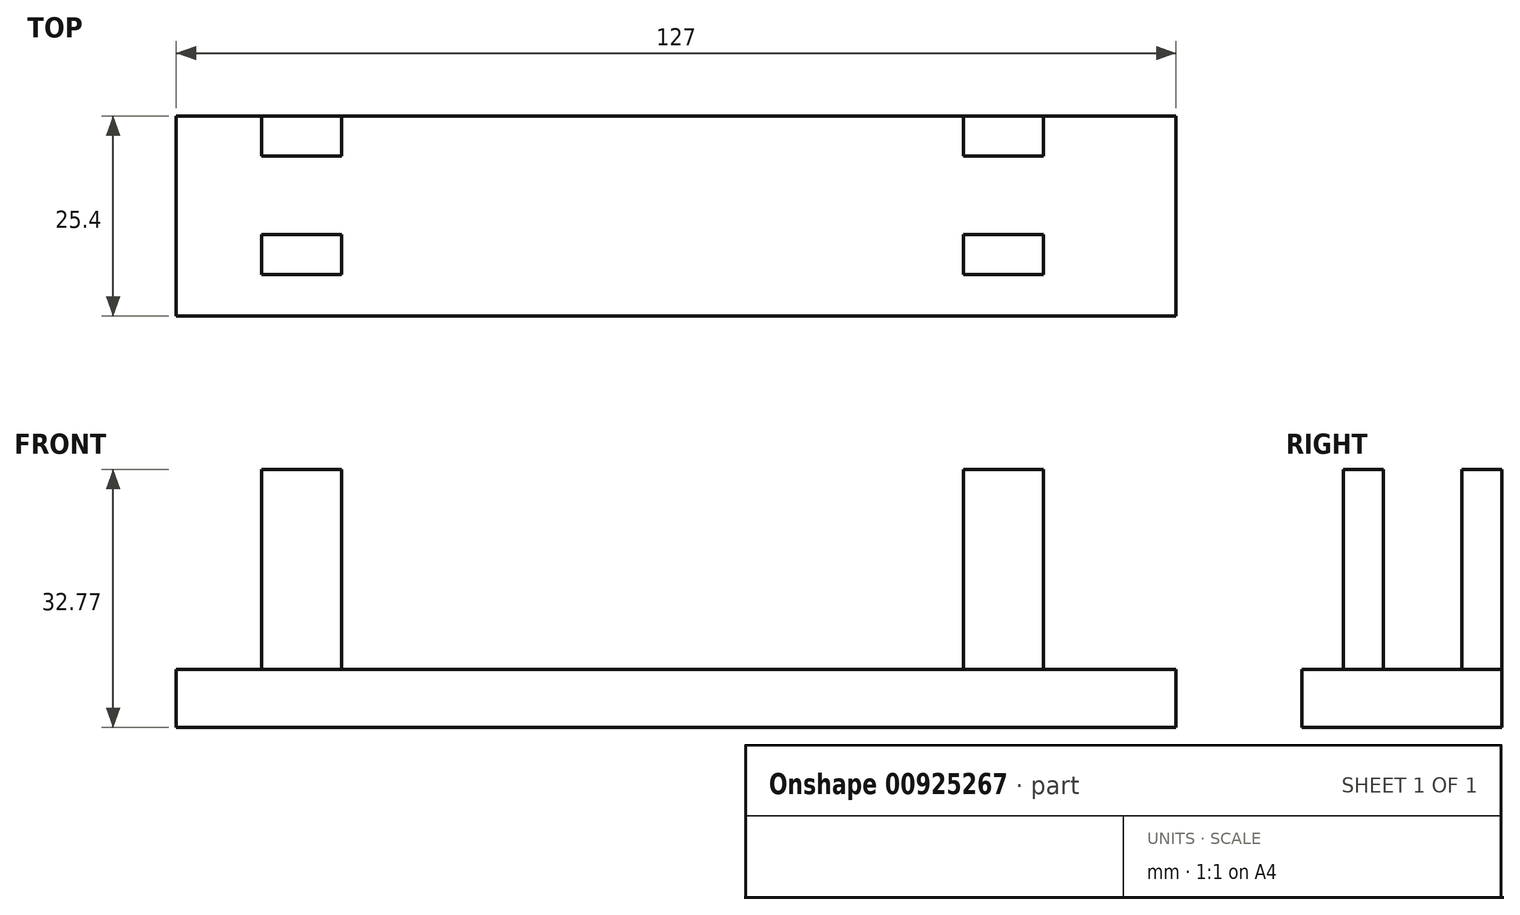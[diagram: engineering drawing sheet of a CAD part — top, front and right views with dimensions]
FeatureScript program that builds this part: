
annotation { "Feature Type Name" : "Feature", "Feature Type Description" : "" }
export const myFeature = defineFeature(function(context is Context, id is Id, definition is map)
    precondition{}
    {
        {
            var Q0;
            Q0=qCreatedBy(makeId("Top.planeOp"),FACE);
            var sketch = newSketch(context, id + "F0", { "sketchPlane" : qUnion([Q0])});
            skLineSegment(sketch, "E0.bottom", {"start": v(-60.5, 10.07) * mm, "end": v(66.5, 10.07) * mm});
            skLineSegment(sketch, "E0.top", {"start": v(-60.5, -15.33) * mm, "end": v(66.5, -15.33) * mm});
            skLineSegment(sketch, "E0.left", {"start": v(-60.5, 10.07) * mm, "end": v(-60.5, -15.33) * mm});
            skLineSegment(sketch, "E0.right", {"start": v(66.5, 10.07) * mm, "end": v(66.5, -15.33) * mm});
            skSolve(sketch);
        }
        {
            var Q0;
            Q0=makeQuery(id+"F0.imprint","IMPRINT",FACE,{"disambiguationData":[TD([[makeQuery(id+"F0.imprint","IMPRINT",EDGE,{"derivedFrom":sQuery(id+"F0.wireOp",EDGE,"E0.bottom")}),-1.0]])]});
            extrude(context, id + "F1", {"entities" : qUnion([Q0]), "depth" : 7.37 * mm, "offsetDistance" : 25.4 * mm});
        }
        {
            var Q0;
            Q0=makeQuery(id+"F1.opExtrude","CAP_FACE",FACE,{"disambiguationData":[OSD([sQuery(id+"F0.wireOp",EDGE,"E0.bottom"),sQuery(id+"F0.wireOp",EDGE,"E0.top"),sQuery(id+"F0.wireOp",EDGE,"E0.left"),sQuery(id+"F0.wireOp",EDGE,"E0.right")])],"isStart":false});
            var sketch = newSketch(context, id + "F2", { "sketchPlane" : qUnion([Q0])});
            skLineSegment(sketch, "E1.bottom", {"start": v(-49.64, 10.07) * mm, "end": v(-39.48, 10.07) * mm});
            skLineSegment(sketch, "E1.top", {"start": v(-49.64, 4.99) * mm, "end": v(-39.48, 4.99) * mm});
            skLineSegment(sketch, "E1.left", {"start": v(-49.64, 10.07) * mm, "end": v(-49.64, 4.99) * mm});
            skLineSegment(sketch, "E1.right", {"start": v(-39.48, 10.07) * mm, "end": v(-39.48, 4.99) * mm});
            skSolve(sketch);
        }
        {
            var Q0;
            Q0=makeQuery(id+"F2.imprint","IMPRINT",FACE,{"disambiguationData":[TD([[makeQuery(id+"F2.imprint","IMPRINT",EDGE,{"derivedFrom":sQuery(id+"F2.wireOp",EDGE,"E1.bottom")}),-1.0]])]});
            extrude(context, id + "F3", {"entities" : qUnion([Q0]), "depth" : 25.4 * mm, "offsetDistance" : 25.4 * mm});
        }
        {
            var Q0;
            Q0=makeQuery(id+"F3.opExtrude","SWEPT_BODY",BODY,{"disambiguationData":[OSD([sQuery(id+"F2.wireOp",EDGE,"E1.bottom"),sQuery(id+"F2.wireOp",EDGE,"E1.top"),sQuery(id+"F2.wireOp",EDGE,"E1.left"),sQuery(id+"F2.wireOp",EDGE,"E1.right")])]});
            var Q1;
            Q1=qCreatedBy(makeId("Right.planeOp"),FACE);
            mirror(context, id + "F4", {"entities" : qUnion([Q0]), "mirrorPlane" : qUnion([Q1])});
        }
        {
            var Q0;
            Q0=makeQuery(id+"F3.opExtrude","SWEPT_BODY",BODY,{"disambiguationData":[OSD([sQuery(id+"F2.wireOp",EDGE,"E1.bottom"),sQuery(id+"F2.wireOp",EDGE,"E1.top"),sQuery(id+"F2.wireOp",EDGE,"E1.left"),sQuery(id+"F2.wireOp",EDGE,"E1.right")])]});
            var Q1;
            Q1=makeQuery(id+"F4.opPattern","COPY",BODY,{"derivedFrom":makeQuery(id+"F3.opExtrude","SWEPT_BODY",BODY,{"disambiguationData":[OSD([sQuery(id+"F2.wireOp",EDGE,"E1.bottom"),sQuery(id+"F2.wireOp",EDGE,"E1.top"),sQuery(id+"F2.wireOp",EDGE,"E1.left"),sQuery(id+"F2.wireOp",EDGE,"E1.right")])]}),"instanceName":"1"});
            var Q2;
            Q2=qCreatedBy(makeId("Front.planeOp"),FACE);
            mirror(context, id + "F5", {"entities" : qUnion([Q0, Q1]), "mirrorPlane" : qUnion([Q2])});
        }
    });
